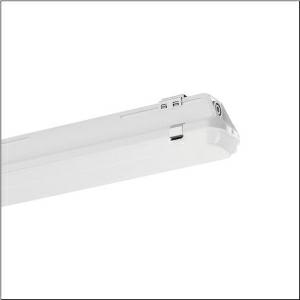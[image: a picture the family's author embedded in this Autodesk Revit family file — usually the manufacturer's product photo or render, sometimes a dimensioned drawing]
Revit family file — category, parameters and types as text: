
# Revit family: monsun_r__11_emergency_51fp10dp468l2_17f5
name_source: partatom
category: Lighting Fixtures
units: mm (PartAtom-declared; Revit-internal decimal feet)

## family parameters
Cut with Voids When Loaded = No
Host = Face
Light Source = No
Part Type = Normal
Room Calculation Point = No
Round Connector Dimension = Use Diameter
Shared = No

## types (1)
- --- (1 x LED, 950 lm, 5.9 W, 4000K)
    Apparent Load = 6 VA
    CIE Flux Codes = 47 77 93 94 100
    Color Rendering = 80
    Color Temperature = 4000K
    Default Elevation = 1800 mm
    Description = Monsun® 11 emergency, damp-proof luminaire, chain hanger, primary optical cover: enclosure, of PMMA, light emission: direct distribution, primary light characteristic: symmetric, installation type: suspended mounting, surface-mounted, horizontal mounting, vertical mounting, LED, rated luminous flux: 6.050lm, luminous efficacy: 192lm/W, light colour: 840, colour temperature: 4000K, control gear: DALI 2, with terminal, 5-pole, max. 2.5mm², mains connection: 220..240V, AC/DC, 0/50..60Hz, rated input power: 32W, luminaire housing, of glass-fibre reinforced polyester, uncoated, bright grey, incl. chain hanger, length: 1.590mm, width: 90mm, height: 88mm, clip for enclosure, of stainless steel (V2A), ceiling mounting element, of stainless steel (V2A), chain hanger, of stainless steel (V2A), protection rating (complete): IP66, insulation class (complete): insulation class I (protective earthing), certification: CE, UKCA, protection symbol: D, impact resistance: IK04, permissible operating ambient temperature: -25..+40°C, standard: EN 50419, EN 60598-2-1, EN 60598-2-22, corresponds to IFS (International Featured Standards) requirements for safety and quality in the food industry, for indoor or canopied outdoor use, no direct snow, no direct sun, no direct rain, LABS conformity tested according to VDMA 24364:2018-05, contact your sales advisor before using the luminaires in applications with unclear chemical exposure, large temperature fluctuations or condensation-forming humidity, packaging unit: 1 piece
    Height = 89 mm
    Lamp = 1 x LED
    Lamp Light Flux = 950 lm
    Lamp Power = 5.9 W
    Lamp count = 1
    Length = 1590 mm
    Luminous efficacy = 161 lm/W
    Manufacturer = Siteco
    ModVariant = No
    Model = 51FP10DP468L2
    Mounting Place = Ceiling
    Mounting Type = Surface mounted
    Number of Poles = 1
    OnlyDefault = Yes
    Power Factor = 1
    Product Name = Monsun® 11 emergency
    Product group = damp-proof luminaire
    ProductGroupID = 300
    Protection Class = Protection class I
    Protection Degree = IP 66
    RLX_Detail_Level = 1
    RLX_Emergency_Light_Flux = 0 lm
    RLX_Emergency_Type = 0
    RLX_Emergency_Type_DB = No
    RlxData = <blob elided: 92505 chars, md5=4087fb8d>
    Socket = socket
    Standby Power = 0 W
    System Light Flux = 950 lm
    System Power = 6 W
    Type Comments = : DC mode (central or group accumulator) initial emergency light level
    Type Image = l_1349237.jpg
    URL = http://relux.com
    VarID = @adj_017922
    Voltage = 0 V
    Weight = 0.00 kg
    Width = 90 mm

## geometry (parser evidence)
native form markers: Blend x4, Sweep x12
no freeform markers — native parametric forms only
